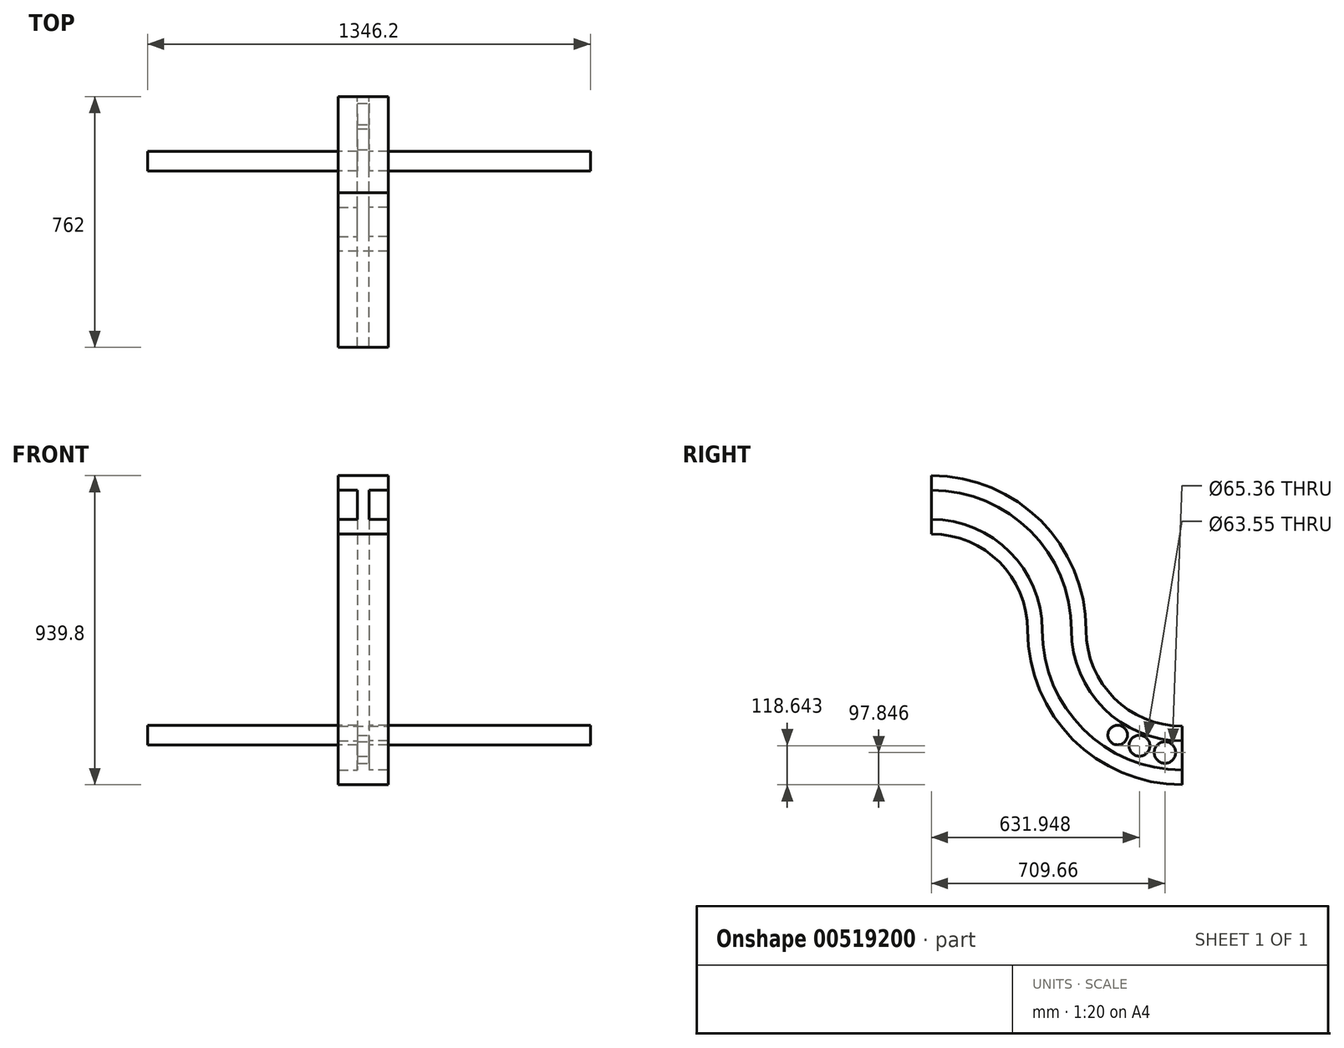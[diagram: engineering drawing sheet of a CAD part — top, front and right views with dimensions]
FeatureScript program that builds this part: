
annotation { "Feature Type Name" : "Feature", "Feature Type Description" : "" }
export const myFeature = defineFeature(function(context is Context, id is Id, definition is map)
    precondition{}
    {
        {
            var Q0;
            Q0=qCreatedBy(makeId("Front.planeOp"),FACE);
            var sketch = newSketch(context, id + "F0", { "sketchPlane" : qUnion([Q0])});
            skLineSegment(sketch, "E0", {"start": v(0, 88.9) * mm, "end": v(76.2, 88.9) * mm});
            skLineSegment(sketch, "E1", {"start": v(76.2, 88.9) * mm, "end": v(76.2, 44.45) * mm});
            skLineSegment(sketch, "E2", {"start": v(76.2, 44.45) * mm, "end": v(17.37, 44.45) * mm});
            skLineSegment(sketch, "E3", {"start": v(0, 88.9) * mm, "end": v(0, -88.9) * mm, "construction": true});
            skLineSegment(sketch, "E4", {"start": v(-17.37, 0) * mm, "end": v(17.37, 0) * mm, "construction": true});
            skLineSegment(sketch, "E5", {"start": v(17.37, 0) * mm, "end": v(17.37, 44.45) * mm});
            skLineSegment(sketch, "E6.MirrorCS", {"start": v(0, 88.9) * mm, "end": v(-76.2, 88.9) * mm});
            skLineSegment(sketch, "E7.MirrorCS", {"start": v(-76.2, 88.9) * mm, "end": v(-76.2, 44.45) * mm});
            skLineSegment(sketch, "E8.MirrorCS", {"start": v(-17.37, 0) * mm, "end": v(-17.37, 44.45) * mm});
            skLineSegment(sketch, "E9.MirrorCS", {"start": v(-76.2, 44.45) * mm, "end": v(-17.37, 44.45) * mm});
            skLineSegment(sketch, "E10.MirrorCS", {"start": v(0, -88.9) * mm, "end": v(-76.2, -88.9) * mm});
            skLineSegment(sketch, "E11.MirrorCS", {"start": v(-76.2, -88.9) * mm, "end": v(-76.2, -44.45) * mm});
            skLineSegment(sketch, "E12.MirrorCS", {"start": v(-76.2, -44.45) * mm, "end": v(-17.37, -44.45) * mm});
            skLineSegment(sketch, "E13.MirrorCS", {"start": v(-17.37, 0) * mm, "end": v(-17.37, -44.45) * mm});
            skLineSegment(sketch, "E14.MirrorCS", {"start": v(76.2, -44.45) * mm, "end": v(17.37, -44.45) * mm});
            skLineSegment(sketch, "E15.MirrorCS", {"start": v(0, -88.9) * mm, "end": v(76.2, -88.9) * mm});
            skLineSegment(sketch, "E16.MirrorCS", {"start": v(17.37, 0) * mm, "end": v(17.37, -44.45) * mm});
            skLineSegment(sketch, "E17.MirrorCS", {"start": v(76.2, -88.9) * mm, "end": v(76.2, -44.45) * mm});
            skSolve(sketch);
        }
        {
            var Q0;
            Q0=qCreatedBy(makeId("Right.planeOp"),FACE);
            var sketch = newSketch(context, id + "F1", { "sketchPlane" : qUnion([Q0])});
            skArc(sketch, "E18", {"start": v(0, 0) * mm, "mid": v(269.4, -111.6) * mm, "end": v(381, -381) * mm});
            skArc(sketch, "E19", {"start": v(381, -381) * mm, "mid": v(492.6, -650.4) * mm, "end": v(762, -762) * mm});
            skSolve(sketch);
        }
        {
            var Q0;
            Q0=makeQuery(id+"F0.imprint","IMPRINT",FACE,{"disambiguationData":[TD([[makeQuery(id+"F0.imprint","IMPRINT",EDGE,{"derivedFrom":sQuery(id+"F0.wireOp",EDGE,"E0")}),-1.0]])]});
            var Q1;
            Q1=sQuery(id+"F1.wireOp",EDGE,"E18");
            var Q2;
            Q2=sQuery(id+"F1.wireOp",EDGE,"E19");
            sweep(context, id + "F2", {"profiles" : qUnion([Q0]), "path" : qUnion([Q1, Q2])});
        }
        {
            var Q0;
            Q0=makeQuery(id+"F2.opSweep","SWEPT_FACE",FACE,{"disambiguationData":[OSD([sQuery(id+"F0.wireOp",EDGE,"E5"),sQuery(id+"F0.wireOp",EDGE,"E16.MirrorCS"),sQuery(id+"F1.wireOp",EDGE,"E18")])]});
            var sketch = newSketch(context, id + "F3", { "sketchPlane" : qUnion([Q0])});
            skCircle(sketch, "E20", {"center": v(565.87, -699.9) * mm, "radius": 29.7 * mm});
            skCircle(sketch, "E21", {"center": v(636.57, -732.46) * mm, "radius": 29.26 * mm});
            skCircle(sketch, "E22", {"center": v(715.57, -753.86) * mm, "radius": 30.1 * mm});
            skSolve(sketch);
        }
        {
            var Q0;
            Q0=makeQuery(id+"F3.imprint","IMPRINT",FACE,{"disambiguationData":[TD([[makeQuery(id+"F3.imprint","IMPRINT",EDGE,{"derivedFrom":sQuery(id+"F3.wireOp",EDGE,"E20")}),1.0]])]});
            extrude(context, id + "F4", {"entities" : qUnion([Q0]), "operationType" : NewBodyOperationType.ADD, "endBound" : BoundingType.SYMMETRIC, "depth" : 1346.2 * mm});
        }
        {
            var Q0;
            Q0=makeQuery(id+"F2.opSweep","SWEPT_FACE",FACE,{"disambiguationData":[OSD([sQuery(id+"F0.wireOp",EDGE,"E5"),sQuery(id+"F0.wireOp",EDGE,"E16.MirrorCS"),sQuery(id+"F1.wireOp",EDGE,"E18")])]});
            var sketch = newSketch(context, id + "F5", { "sketchPlane" : qUnion([Q0])});
            skCircle(sketch, "E23", {"center": v(631.95, -732.26) * mm, "radius": 31.78 * mm});
            skCircle(sketch, "E24", {"center": v(709.66, -753.05) * mm, "radius": 32.68 * mm});
            skSolve(sketch);
        }
        {
            var Q0;
            Q0=makeQuery(id+"F5.imprint","IMPRINT",FACE,{"disambiguationData":[TD([[makeQuery(id+"F5.imprint","IMPRINT",EDGE,{"derivedFrom":sQuery(id+"F5.wireOp",EDGE,"E23")}),1.0]])]});
            var Q1;
            Q1=makeQuery(id+"F5.imprint","IMPRINT",FACE,{"disambiguationData":[TD([[makeQuery(id+"F5.imprint","IMPRINT",EDGE,{"derivedFrom":sQuery(id+"F5.wireOp",EDGE,"E24")}),1.0]])]});
            extrude(context, id + "F6", {"entities" : qUnion([Q0, Q1]), "operationType" : NewBodyOperationType.REMOVE, "endBound" : BoundingType.THROUGH_ALL, "oppositeDirection" : true, "depth" : 25.4 * mm});
        }
        {
            var Q0;
            Q0=makeQuery(id+"F0.imprint","IMPRINT",FACE,{"disambiguationData":[TD([[makeQuery(id+"F0.imprint","IMPRINT",EDGE,{"derivedFrom":sQuery(id+"F0.wireOp",EDGE,"E0")}),-1.0]])]});
            var Q1;
            Q1=sQuery(id+"F1.wireOp",EDGE,"E18");
            var Q2;
            Q2=sQuery(id+"F1.wireOp",EDGE,"E19");
            sweep(context, id + "F7", {"profiles" : qUnion([Q0]), "path" : qUnion([Q1, Q2])});
        }
    });
